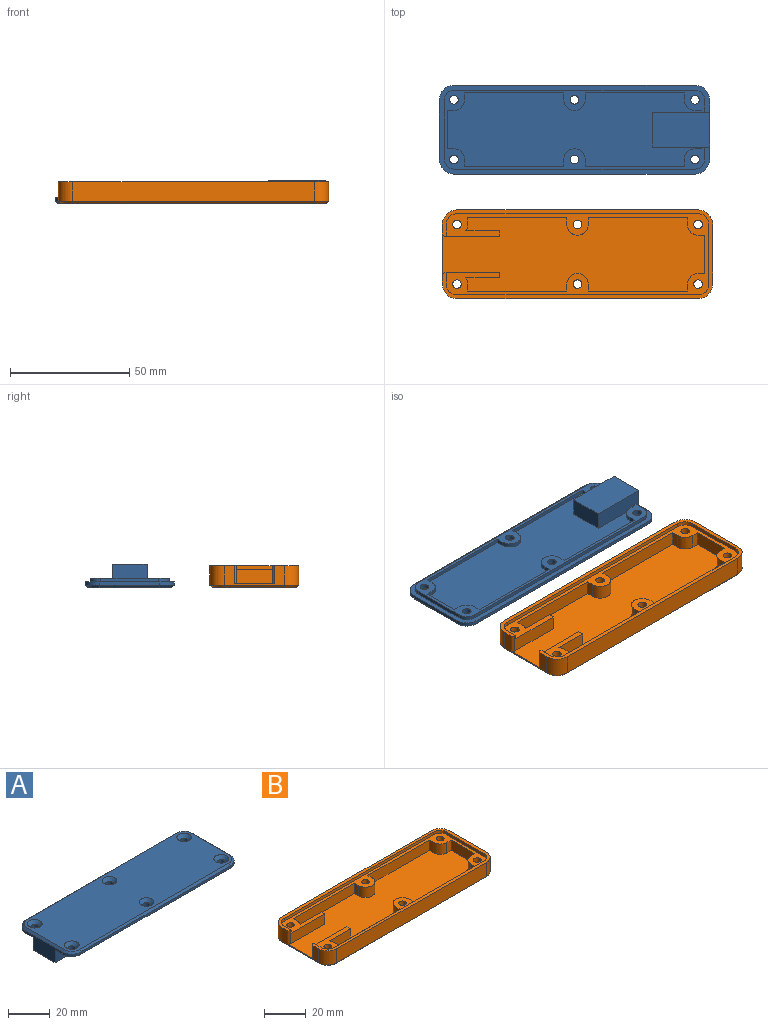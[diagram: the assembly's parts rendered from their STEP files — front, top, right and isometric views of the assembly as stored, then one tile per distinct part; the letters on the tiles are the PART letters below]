
ASSEMBLY  parts=2 mates=1
PART A: 70 faces, bbox 113.2x37.2x9.8 mm
  f0: plane 1.6x0.7mm, normal (1,0,0), area 1.1mm2, adj f48,f50,f51,f67
  f1: plane 4.8x1.6mm, normal (-1,0,0), area 7.7mm2, adj f17,f43,f50,f67
  f2: plane 101x1.4mm, normal (0,1,0), area 141.4mm2, adj f3,f14,f17,f65
  f3: cylinder r=6.1mm len=6.1mm, axis (0,0,-1), area 13.4mm2, adj f2,f4,f17,f63
  f4: plane 25x8.8mm, normal (-1,0,0), area 143mm2, adj f3,f5,f17,f61,f66,f67,f69
  f5: cylinder r=6.1mm len=6.1mm, axis (0,0,-1), area 13.4mm2, adj f4,f6,f17,f59
  f6: plane 101x1.4mm, normal (0,-1,0), area 141.4mm2, adj f5,f7,f17,f58
  f7: cylinder r=6.1mm len=6.1mm, axis (0,0,-1), area 13.4mm2, adj f6,f8,f17,f60
  f8: plane 25x1.4mm, normal (1,0,0), area 35mm2, adj f7,f14,f17,f62
  f9: cylinder r=1.8mm len=3.6mm, axis (0,0,-1), area 26mm2, adj f50,f56
  f10: cylinder r=1.8mm len=3.6mm, axis (0,0,-1), area 26mm2, adj f50,f55
  f11: cylinder r=1.8mm len=3.6mm, axis (0,0,-1), area 26mm2, adj f50,f53
  f12: cylinder r=1.8mm len=3.6mm, axis (0,0,-1), area 26mm2, adj f50,f52
  f13: cylinder r=1.8mm len=3.6mm, axis (0,0,-1), area 26mm2, adj f50,f54
  f14: cylinder r=6.1mm len=6.1mm, axis (0,0,-1), area 13.4mm2, adj f2,f8,f17,f64
  f15: cylinder r=1.8mm len=3.6mm, axis (0,0,-1), area 26mm2, adj f50,f57
  f16: plane 111.2x35.2mm, normal (0,0,1), area 3661mm2, adj f52,f53,f54,f55,f56,f57,f58,f59
  f17: plane 113.2x37.2mm, normal (0,0,-1), area 541.8mm2, adj f1,f2,f3,f4,f5,f6,f7,f8
  f18: plane 1.6x0.7mm, normal (1,0,0), area 1.1mm2, adj f19,f50,f51,f66
  f19: plane 2.9x1.6mm, normal (0,-1,0), area 4.6mm2, adj f18,f20,f50,f51
  f20: cylinder r=4.5mm len=4.5mm, axis (0,0,1), area 11.3mm2, adj f19,f21,f50,f51
  f21: plane 2.9x1.6mm, normal (1,0,0), area 4.6mm2, adj f20,f22,f50,f51
  f22: plane 41.5x1.6mm, normal (0,-1,0), area 66.4mm2, adj f21,f23,f50,f51
  f23: plane 2.9x1.6mm, normal (-1,0,0), area 4.6mm2, adj f22,f24,f50,f51
  f24: cylinder r=4.5mm len=9mm, axis (0,0,1), area 22.6mm2, adj f23,f25,f50,f51
  f25: plane 2.9x1.6mm, normal (1,0,0), area 4.6mm2, adj f24,f26,f50,f51
  f26: plane 41.5x1.6mm, normal (0,-1,0), area 66.4mm2, adj f25,f27,f50,f51
  f27: plane 2.9x1.6mm, normal (-1,0,0), area 4.6mm2, adj f26,f28,f50,f51
  f28: cylinder r=4.5mm len=4.5mm, axis (0,0,1), area 11.3mm2, adj f27,f29,f50,f51
  f29: plane 2.9x1.6mm, normal (0,-1,0), area 4.6mm2, adj f28,f30,f50,f51
  f30: plane 16x1.6mm, normal (-1,0,0), area 25.6mm2, adj f29,f31,f50,f51
  f31: plane 2.9x1.6mm, normal (0,1,0), area 4.6mm2, adj f30,f32,f50,f51
  f32: cylinder r=4.5mm len=4.5mm, axis (0,0,1), area 11.3mm2, adj f31,f33,f50,f51
  f33: plane 2.9x1.6mm, normal (-1,0,0), area 4.6mm2, adj f32,f34,f50,f51
  f34: plane 41.5x1.6mm, normal (0,1,0), area 66.4mm2, adj f33,f35,f50,f51
  f35: plane 2.9x1.6mm, normal (1,0,0), area 4.6mm2, adj f34,f36,f50,f51
  f36: cylinder r=4.5mm len=9mm, axis (0,0,1), area 22.6mm2, adj f35,f37,f50,f51
  f37: plane 2.9x1.6mm, normal (-1,0,0), area 4.6mm2, adj f36,f38,f50,f51
  f38: plane 41.5x1.6mm, normal (0,1,0), area 66.4mm2, adj f37,f39,f50,f51
  f39: plane 2.9x1.6mm, normal (1,0,0), area 4.6mm2, adj f38,f40,f50,f51
  f40: cylinder r=4.5mm len=4.5mm, axis (0,0,1), area 11.3mm2, adj f39,f48,f50,f51
  f41: cylinder r=4.5mm len=4.5mm, axis (0,0,1), area 11.3mm2, adj f17,f42,f49,f50
  f42: plane 4.8x1.6mm, normal (-1,0,0), area 7.7mm2, adj f17,f41,f50,f66
  f43: cylinder r=4.5mm len=4.5mm, axis (0,0,1), area 11.3mm2, adj f1,f17,f44,f50
  f44: plane 100.2x1.6mm, normal (0,-1,0), area 160.3mm2, adj f17,f43,f45,f50
  f45: cylinder r=4.5mm len=4.5mm, axis (0,0,1), area 11.3mm2, adj f17,f44,f46,f50
  f46: plane 24.2x1.6mm, normal (1,0,0), area 38.7mm2, adj f17,f45,f47,f50
  f47: cylinder r=4.5mm len=4.5mm, axis (0,0,1), area 11.3mm2, adj f17,f46,f49,f50
  f48: plane 2.9x1.6mm, normal (0,1,0), area 4.6mm2, adj f0,f40,f50,f51
  f49: plane 100.2x1.6mm, normal (0,1,0), area 160.3mm2, adj f17,f41,f47,f50
  f50: plane 109.2x33.2mm, normal (0,0,-1), area 557.5mm2, adj f0,f1,f9,f10,f11,f12,f13,f15
  f51: plane 106.8x30.8mm, normal (0,0,-1), area 2668.3mm2, adj f0,f18,f19,f20,f21,f22,f23,f24
  f52: cone r=1.8mm half-angle=45deg, axis (0,0,1), area 40mm2, adj f12,f16
  f53: cone r=1.8mm half-angle=45deg, axis (0,0,1), area 40mm2, adj f11,f16
  f54: cone r=1.8mm half-angle=45deg, axis (0,0,1), area 40mm2, adj f13,f16
  f55: cone r=1.8mm half-angle=45deg, axis (0,0,1), area 40mm2, adj f10,f16
  f56: cone r=1.8mm half-angle=45deg, axis (0,0,1), area 40mm2, adj f9,f16
  f57: cone r=1.8mm half-angle=45deg, axis (0,0,1), area 40mm2, adj f15,f16
  f58: plane 101x1mm, normal (0,-0.71,0.71), area 142.8mm2, adj f6,f16,f59,f60
  f59: cone r=5.1mm half-angle=45deg, axis (0,0,-1), area 12.4mm2, adj f5,f16,f58,f61
  f60: cone r=5.1mm half-angle=45deg, axis (0,0,-1), area 12.4mm2, adj f7,f16,f58,f62
  f61: plane 25x1mm, normal (-0.71,0,0.71), area 35.4mm2, adj f4,f16,f59,f63
  f62: plane 25x1mm, normal (0.71,0,0.71), area 35.4mm2, adj f8,f16,f60,f64
  f63: cone r=5.1mm half-angle=45deg, axis (0,0,-1), area 12.4mm2, adj f3,f16,f61,f65
  f64: cone r=5.1mm half-angle=45deg, axis (0,0,-1), area 12.4mm2, adj f14,f16,f62,f65
  f65: plane 101x1mm, normal (0,0.71,0.71), area 142.8mm2, adj f2,f16,f63,f64
  f66: plane 24x7.4mm, normal (0,1,0), area 175.7mm2, adj f4,f17,f18,f42,f50,f51,f68,f69
  f67: plane 24x7.4mm, normal (0,-1,0), area 175.7mm2, adj f0,f1,f4,f17,f50,f51,f68,f69
  f68: plane 14.6x7.4mm, normal (1,0,0), area 108mm2, adj f51,f66,f67,f69
  f69: plane 24x14.6mm, normal (0,0,-1), area 350.4mm2, adj f4,f66,f67,f68
PART B: 106 faces, bbox 113.2x37.2x9.2 mm
  f0: cylinder r=1.8mm len=3.6mm, axis (0,0,1), area 29.4mm2, adj f43,f105
  f1: cylinder r=1.8mm len=3.6mm, axis (0,0,1), area 29.4mm2, adj f43,f77
  f2: cylinder r=1.8mm len=3.6mm, axis (0,0,1), area 29.4mm2, adj f43,f84
  f3: cylinder r=1.8mm len=3.6mm, axis (0,0,1), area 29.4mm2, adj f43,f70
  f4: cylinder r=1.8mm len=3.6mm, axis (0,0,1), area 29.4mm2, adj f43,f91
  f5: cylinder r=1.8mm len=3.6mm, axis (0,0,1), area 29.4mm2, adj f43,f98
  f6: plane 110x30.8mm, normal (0,0,1), area 2941.9mm2, adj f9,f16,f17,f18,f19,f20,f21,f22
  f7: plane 101x8.2mm, normal (0,1,0), area 828.2mm2, adj f8,f14,f53,f54
  f8: cylinder r=6.1mm len=8.2mm, axis (0,0,1), area 78.6mm2, adj f7,f9,f53,f55
  f9: plane 25x8.2mm, normal (-1,0,0), area 75.8mm2, adj f6,f8,f10,f53,f57,f62,f63
  f10: cylinder r=6.1mm len=8.2mm, axis (0,0,1), area 78.6mm2, adj f9,f11,f53,f59
  f11: plane 101x8.2mm, normal (0,-1,0), area 828.2mm2, adj f10,f12,f53,f61
  f12: cylinder r=6.1mm len=8.2mm, axis (0,0,1), area 78.6mm2, adj f11,f13,f53,f60
  f13: plane 25x8.2mm, normal (1,0,0), area 205mm2, adj f12,f14,f53,f58
  f14: cylinder r=6.1mm len=8.2mm, axis (0,0,1), area 78.6mm2, adj f7,f13,f53,f56
  f15: plane 111.2x35.2mm, normal (0,0,-1), area 3704.9mm2, adj f54,f55,f56,f57,f58,f59,f60,f61
  f16: plane 23x7.6mm, normal (0,-1,0), area 139mm2, adj f6,f17,f43,f45,f53,f63
  f17: plane 6x2.4mm, normal (1,0,0), area 14.4mm2, adj f6,f16,f18,f43
  f18: plane 14.23x6mm, normal (0,1,0), area 85.4mm2, adj f6,f17,f19,f43
  f19: cylinder r=4.5mm len=6mm, axis (0,0,-1), area 16.6mm2, adj f6,f18,f20,f43
  f20: plane 6x2.9mm, normal (1,0,0), area 17.4mm2, adj f6,f19,f21,f43
  f21: plane 41.5x6mm, normal (0,-1,0), area 249mm2, adj f6,f20,f22,f43
  f22: plane 6x2.9mm, normal (-1,0,0), area 17.4mm2, adj f6,f21,f23,f43
  f23: cylinder r=4.5mm len=9mm, axis (0,0,-1), area 84.8mm2, adj f6,f22,f24,f43
  f24: plane 6x2.9mm, normal (1,0,0), area 17.4mm2, adj f6,f23,f25,f43
  f25: plane 41.5x6mm, normal (0,-1,0), area 249mm2, adj f6,f24,f26,f43
  f26: plane 6x2.9mm, normal (-1,0,0), area 17.4mm2, adj f6,f25,f27,f43
  f27: cylinder r=4.5mm len=6mm, axis (0,0,-1), area 42.4mm2, adj f6,f26,f28,f43
  f28: plane 6x2.9mm, normal (0,-1,0), area 17.4mm2, adj f6,f27,f29,f43
  f29: plane 16x6mm, normal (-1,0,0), area 96mm2, adj f6,f28,f30,f43
  f30: plane 6x2.9mm, normal (0,1,0), area 17.4mm2, adj f6,f29,f31,f43
  f31: cylinder r=4.5mm len=6mm, axis (0,0,-1), area 42.4mm2, adj f6,f30,f32,f43
  f32: plane 6x2.9mm, normal (-1,0,0), area 17.4mm2, adj f6,f31,f33,f43
  f33: plane 41.5x6mm, normal (0,1,0), area 249mm2, adj f6,f32,f34,f43
  f34: plane 6x2.9mm, normal (1,0,0), area 17.4mm2, adj f6,f33,f35,f43
  f35: cylinder r=4.5mm len=9mm, axis (0,0,-1), area 84.8mm2, adj f6,f34,f36,f43
  f36: plane 6x2.9mm, normal (-1,0,0), area 17.4mm2, adj f6,f35,f37,f43
  f37: plane 41.5x6mm, normal (0,1,0), area 249mm2, adj f6,f36,f38,f43
  f38: plane 6x2.9mm, normal (1,0,0), area 17.4mm2, adj f6,f37,f39,f43
  f39: cylinder r=4.5mm len=6mm, axis (0,0,-1), area 16.6mm2, adj f6,f38,f40,f43
  f40: plane 14.23x6mm, normal (0,-1,0), area 85.4mm2, adj f6,f39,f41,f43
  f41: plane 6x2.4mm, normal (1,0,0), area 14.4mm2, adj f6,f40,f42,f43
  f42: plane 23x7.6mm, normal (0,1,0), area 139mm2, adj f6,f41,f43,f46,f53,f62
  f43: plane 110x34mm, normal (0,0,1), area 744.6mm2, adj f0,f1,f2,f3,f4,f5,f16,f17
  f44: plane 101x1.6mm, normal (0,-1,0), area 161.6mm2, adj f43,f49,f50,f53
  f45: plane 5x1.6mm, normal (1,0,0), area 8mm2, adj f16,f43,f49,f53
  f46: plane 5x1.6mm, normal (1,0,0), area 8mm2, adj f42,f43,f52,f53
  f47: plane 101x1.6mm, normal (0,1,0), area 161.6mm2, adj f43,f51,f52,f53
  f48: plane 25x1.6mm, normal (-1,0,0), area 40mm2, adj f43,f50,f51,f53
  f49: cylinder r=4.5mm len=4.5mm, axis (0,0,-1), area 11.3mm2, adj f43,f44,f45,f53
  f50: cylinder r=4.5mm len=4.5mm, axis (0,0,-1), area 11.3mm2, adj f43,f44,f48,f53
  f51: cylinder r=4.5mm len=4.5mm, axis (0,0,-1), area 11.3mm2, adj f43,f47,f48,f53
  f52: cylinder r=4.5mm len=4.5mm, axis (0,0,-1), area 11.3mm2, adj f43,f46,f47,f53
  f53: plane 113.2x37.2mm, normal (0,0,1), area 431.5mm2, adj f7,f8,f9,f10,f11,f12,f13,f14
  f54: plane 101x1mm, normal (0,0.71,-0.71), area 142.8mm2, adj f7,f15,f55,f56
  f55: cone r=5.1mm half-angle=45deg, axis (0,0,1), area 12.4mm2, adj f8,f15,f54,f57
  f56: cone r=5.1mm half-angle=45deg, axis (0,0,1), area 12.4mm2, adj f14,f15,f54,f58
  f57: plane 25x1mm, normal (-0.71,0,-0.71), area 35.4mm2, adj f9,f15,f55,f59
  f58: plane 25x1mm, normal (0.71,0,-0.71), area 35.4mm2, adj f13,f15,f56,f60
  f59: cone r=6.1mm half-angle=45deg, axis (0,0,1), area 12.4mm2, adj f10,f15,f57,f61
  f60: cone r=5.1mm half-angle=45deg, axis (0,0,1), area 12.4mm2, adj f12,f15,f58,f61
  f61: plane 101x1mm, normal (0,-0.71,-0.71), area 142.8mm2, adj f11,f15,f59,f60
  f62: plane 7.6x1mm, normal (-0.71,0.71,0), area 10.7mm2, adj f6,f9,f42,f53
  f63: plane 7.6x1mm, normal (-0.71,-0.71,0), area 10.7mm2, adj f6,f9,f16,f53
  f64: plane 5x3mm, normal (-0.87,0.5,0), area 17.3mm2, adj f15,f65,f69,f70
  f65: plane 5x3.46mm, normal (0,1,0), area 17.3mm2, adj f15,f64,f66,f70
  f66: plane 5x3mm, normal (0.87,0.5,0), area 17.3mm2, adj f15,f65,f67,f70
  f67: plane 5x3mm, normal (0.87,-0.5,0), area 17.3mm2, adj f15,f66,f68,f70
  f68: plane 5x3.46mm, normal (0,-1,0), area 17.3mm2, adj f15,f67,f69,f70
  f69: plane 5x3mm, normal (-0.87,-0.5,0), area 17.3mm2, adj f15,f64,f68,f70
  f70: plane 6.93x6mm, normal (0,0,-1), area 21mm2, adj f3,f64,f65,f66,f67,f68,f69
  f71: plane 5x3mm, normal (-0.87,0.5,0), area 17.3mm2, adj f15,f72,f76,f77
  f72: plane 5x3.46mm, normal (0,1,0), area 17.3mm2, adj f15,f71,f73,f77
  f73: plane 5x3mm, normal (0.87,0.5,0), area 17.3mm2, adj f15,f72,f74,f77
  f74: plane 5x3mm, normal (0.87,-0.5,0), area 17.3mm2, adj f15,f73,f75,f77
  f75: plane 5x3.46mm, normal (0,-1,0), area 17.3mm2, adj f15,f74,f76,f77
  f76: plane 5x3mm, normal (-0.87,-0.5,0), area 17.3mm2, adj f15,f71,f75,f77
  f77: plane 6.93x6mm, normal (0,0,-1), area 21mm2, adj f1,f71,f72,f73,f74,f75,f76
  f78: plane 5x3mm, normal (-0.87,0.5,0), area 17.3mm2, adj f15,f79,f83,f84
  f79: plane 5x3.46mm, normal (0,1,0), area 17.3mm2, adj f15,f78,f80,f84
  f80: plane 5x3mm, normal (0.87,0.5,0), area 17.3mm2, adj f15,f79,f81,f84
  f81: plane 5x3mm, normal (0.87,-0.5,0), area 17.3mm2, adj f15,f80,f82,f84
  f82: plane 5x3.46mm, normal (0,-1,0), area 17.3mm2, adj f15,f81,f83,f84
  f83: plane 5x3mm, normal (-0.87,-0.5,0), area 17.3mm2, adj f15,f78,f82,f84
  f84: plane 6.93x6mm, normal (0,0,-1), area 21mm2, adj f2,f78,f79,f80,f81,f82,f83
  f85: plane 5x3mm, normal (-0.87,0.5,0), area 17.3mm2, adj f15,f86,f90,f91
  f86: plane 5x3.46mm, normal (0,1,0), area 17.3mm2, adj f15,f85,f87,f91
  f87: plane 5x3mm, normal (0.87,0.5,0), area 17.3mm2, adj f15,f86,f88,f91
  f88: plane 5x3mm, normal (0.87,-0.5,0), area 17.3mm2, adj f15,f87,f89,f91
  f89: plane 5x3.46mm, normal (0,-1,0), area 17.3mm2, adj f15,f88,f90,f91
  f90: plane 5x3mm, normal (-0.87,-0.5,0), area 17.3mm2, adj f15,f85,f89,f91
  f91: plane 6.93x6mm, normal (0,0,-1), area 21mm2, adj f4,f85,f86,f87,f88,f89,f90
  f92: plane 5x3mm, normal (-0.87,0.5,0), area 17.3mm2, adj f15,f93,f97,f98
  f93: plane 5x3.46mm, normal (0,1,0), area 17.3mm2, adj f15,f92,f94,f98
  f94: plane 5x3mm, normal (0.87,0.5,0), area 17.3mm2, adj f15,f93,f95,f98
  f95: plane 5x3mm, normal (0.87,-0.5,0), area 17.3mm2, adj f15,f94,f96,f98
  f96: plane 5x3.46mm, normal (0,-1,0), area 17.3mm2, adj f15,f95,f97,f98
  f97: plane 5x3mm, normal (-0.87,-0.5,0), area 17.3mm2, adj f15,f92,f96,f98
  f98: plane 6.93x6mm, normal (0,0,-1), area 21mm2, adj f5,f92,f93,f94,f95,f96,f97
  f99: plane 5x3mm, normal (-0.87,0.5,0), area 17.3mm2, adj f15,f100,f104,f105
  f100: plane 5x3.46mm, normal (0,1,0), area 17.3mm2, adj f15,f99,f101,f105
  f101: plane 5x3mm, normal (0.87,0.5,0), area 17.3mm2, adj f15,f100,f102,f105
  f102: plane 5x3mm, normal (0.87,-0.5,0), area 17.3mm2, adj f15,f101,f103,f105
  f103: plane 5x3.46mm, normal (0,-1,0), area 17.3mm2, adj f15,f102,f104,f105
  f104: plane 5x3mm, normal (-0.87,-0.5,0), area 17.3mm2, adj f15,f99,f103,f105
  f105: plane 6.93x6mm, normal (0,0,-1), area 21mm2, adj f0,f99,f100,f101,f102,f103,f104
PLACE A rot(axis=(0,1,0),180deg) t=(-1.23,27.3,47.92)mm
PLACE B t=(0.04,-24.93,22.12)mm
MATE planar A.f16 <-> B.f15  axis (0,0,-1) through (-1.23,27.3,20.52)mm
